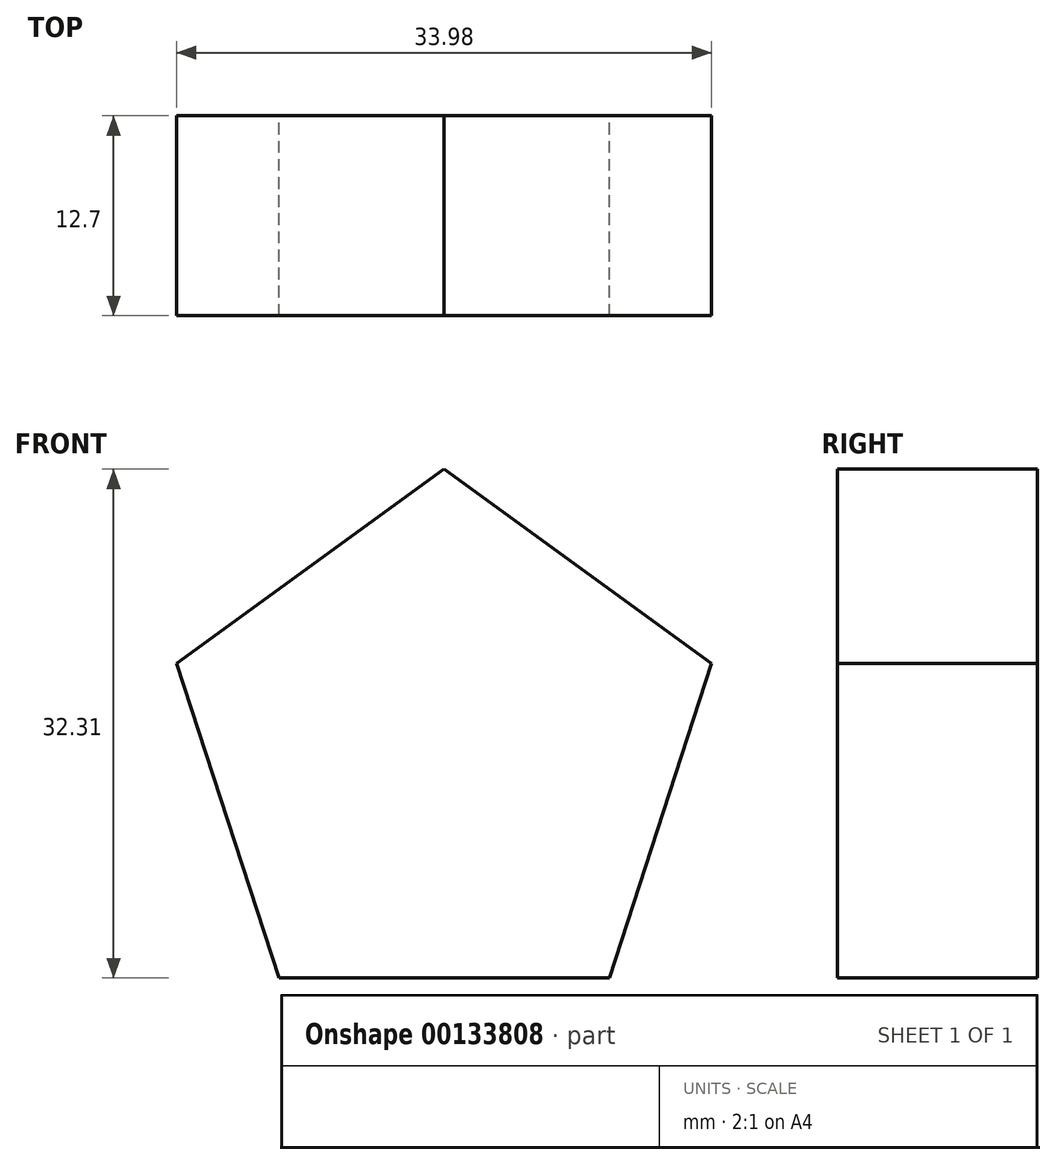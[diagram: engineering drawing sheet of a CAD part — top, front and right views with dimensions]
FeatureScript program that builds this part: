
annotation { "Feature Type Name" : "Feature", "Feature Type Description" : "" }
export const myFeature = defineFeature(function(context is Context, id is Id, definition is map)
    precondition{}
    {
        {
            var Q0;
            Q0=qCreatedBy(makeId("Front.planeOp"),FACE);
            var sketch = newSketch(context, id + "F0", { "sketchPlane" : qUnion([Q0])});
            skCircle(sketch, "E0.cCircle", {"center": v(0, 0) * mm, "radius": 14.45 * mm, "construction": true});
            skLineSegment(sketch, "E0.0", {"start": v(10.5, -14.45) * mm, "end": v(-10.5, -14.45) * mm});
            skLineSegment(sketch, "E0.1", {"start": v(-10.5, -14.45) * mm, "end": v(-16.99, 5.52) * mm});
            skLineSegment(sketch, "E0.2", {"start": v(-16.99, 5.52) * mm, "end": v(0, 17.86) * mm});
            skLineSegment(sketch, "E0.3", {"start": v(0, 17.86) * mm, "end": v(16.99, 5.52) * mm});
            skLineSegment(sketch, "E0.4", {"start": v(16.99, 5.52) * mm, "end": v(10.5, -14.45) * mm});
            skPoint(sketch, "E0.0.midPoint", {"position": v(0, -14.45) * mm});
            skSolve(sketch);
        }
        {
            var Q0;
            Q0 = qSketchRegion(id + "F0", true);
            extrude(context, id + "F1", {"entities" : qUnion([Q0]), "endBound" : BoundingType.SYMMETRIC, "depth" : 12.7 * mm});
        }
    });
